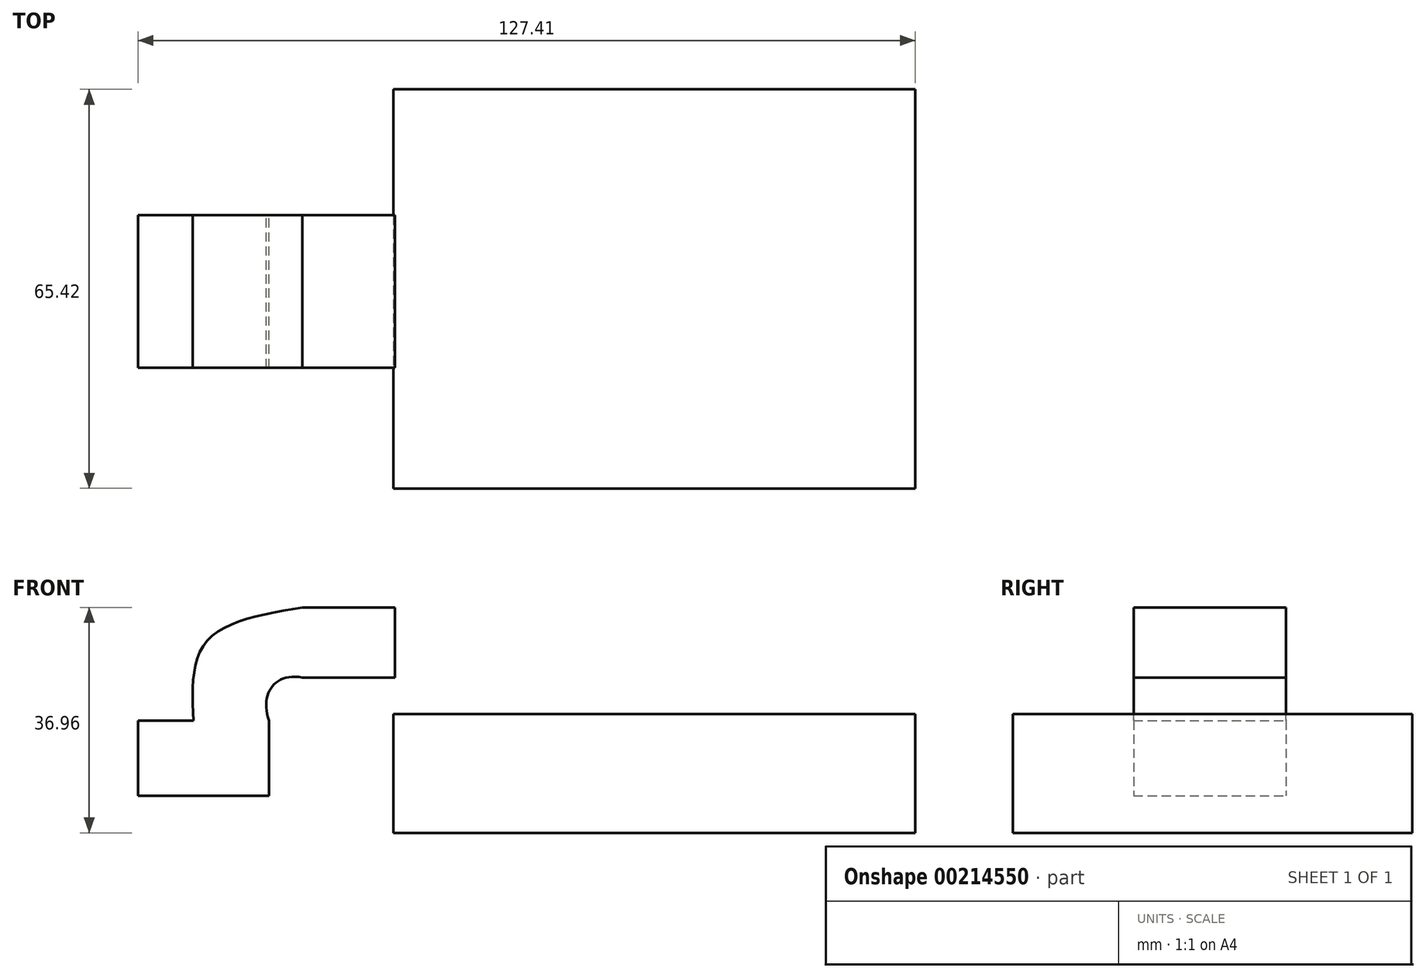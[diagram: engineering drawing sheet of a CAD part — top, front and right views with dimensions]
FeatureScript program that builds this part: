
annotation { "Feature Type Name" : "Feature", "Feature Type Description" : "" }
export const myFeature = defineFeature(function(context is Context, id is Id, definition is map)
    precondition{}
    {
        {
            var Q0;
            Q0=qCreatedBy(makeId("Front.planeOp"),FACE);
            var sketch = newSketch(context, id + "F0", { "sketchPlane" : qUnion([Q0])});
            skLineSegment(sketch, "E0.top", {"start": v(-52.14, 6.08) * mm, "end": v(-30.68, 6.08) * mm});
            skLineSegment(sketch, "E0.left", {"start": v(-52.14, 18.38) * mm, "end": v(-52.14, 6.08) * mm});
            skLineSegment(sketch, "E0.right", {"start": v(-30.68, 18.38) * mm, "end": v(-30.68, 6.08) * mm});
            skLineSegment(sketch, "E1.bottom", {"start": v(-25.18, 36.96) * mm, "end": v(-10, 36.96) * mm});
            skLineSegment(sketch, "E1.top", {"start": v(-25.18, 25.45) * mm, "end": v(-10, 25.45) * mm});
            skLineSegment(sketch, "E1.right", {"start": v(-10, 36.96) * mm, "end": v(-10, 25.45) * mm});
            skFitSpline(sketch, "E2", {"points": [v(-30.68, 18.38) * mm, v(-25.18, 25.45) * mm], "startDerivative": vector(-4.6, 12.9) * mm, "endDerivative": vector(14.04, -2.7) * mm});
            skFitSpline(sketch, "E3", {"points": [v(-25.18, 36.96) * mm, v(-40.96, 31.3) * mm, v(-43.04, 18.38) * mm], "startDerivative": vector(-36.44, -6.16) * mm, "endDerivative": vector(1.5, -31.52) * mm});
            skLineSegment(sketch, "E4", {"start": v(-43.04, 18.38) * mm, "end": v(-52.14, 18.38) * mm});
            skSolve(sketch);
        }
        {
            var Q0;
            Q0 = qSketchRegion(id + "F0", true);
            extrude(context, id + "F1", {"entities" : qUnion([Q0]), "depth" : 25 * mm});
        }
        {
            var Q0;
            Q0=qCreatedBy(makeId("Top.planeOp"),FACE);
            var sketch = newSketch(context, id + "F2", { "sketchPlane" : qUnion([Q0])});
            skLineSegment(sketch, "E5.bottom", {"start": v(-10.26, 20.65) * mm, "end": v(75.27, 20.65) * mm});
            skLineSegment(sketch, "E5.top", {"start": v(-10.26, -44.77) * mm, "end": v(75.27, -44.77) * mm});
            skLineSegment(sketch, "E5.left", {"start": v(-10.26, 20.65) * mm, "end": v(-10.26, -44.77) * mm});
            skLineSegment(sketch, "E5.right", {"start": v(75.27, 20.65) * mm, "end": v(75.27, -44.77) * mm});
            skSolve(sketch);
        }
        {
            var Q0;
            Q0 = qSketchRegion(id + "F2", true);
            extrude(context, id + "F3", {"entities" : qUnion([Q0]), "depth" : 19.5 * mm});
        }
    });
